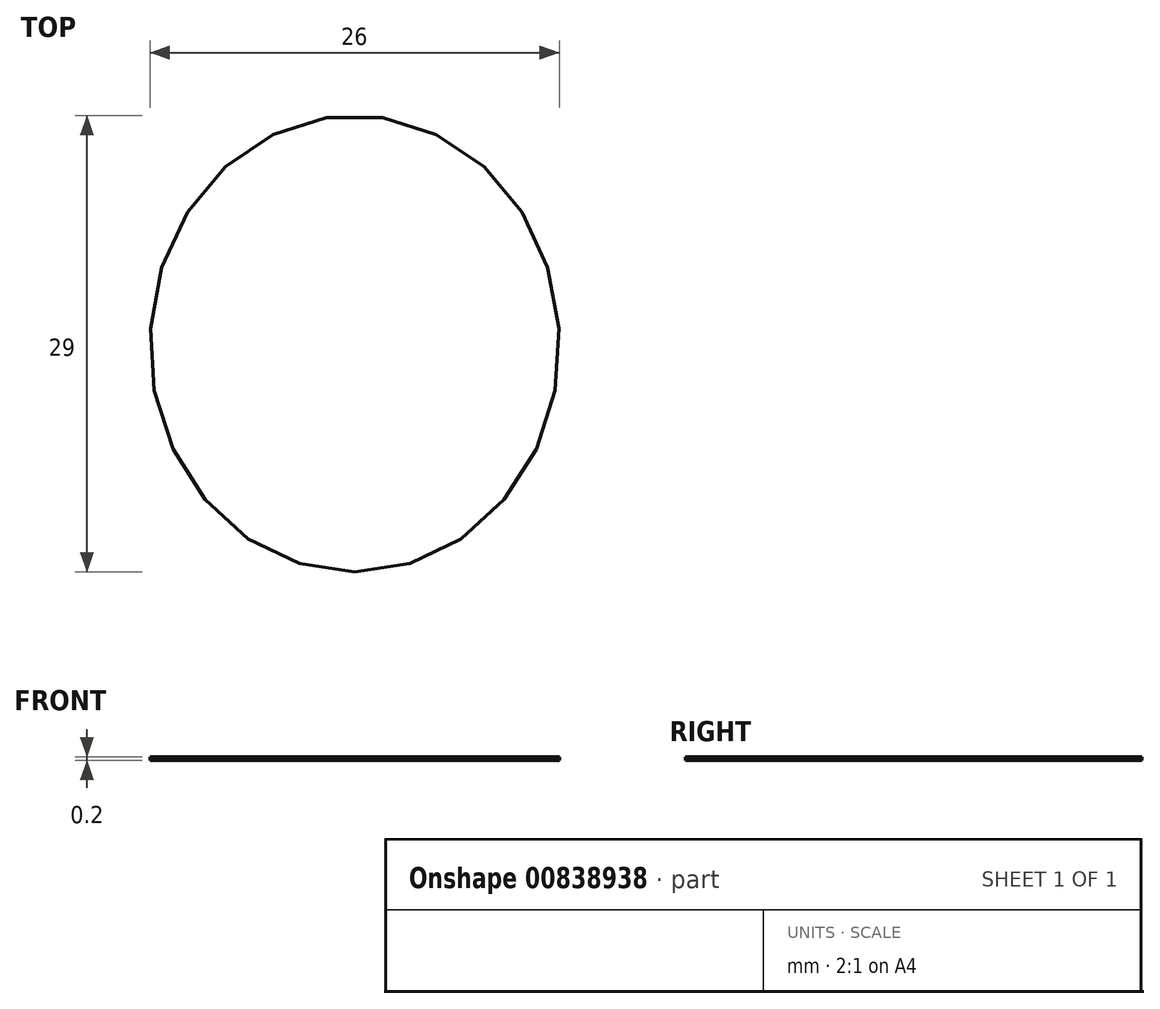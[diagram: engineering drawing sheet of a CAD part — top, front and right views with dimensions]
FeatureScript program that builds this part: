
annotation { "Feature Type Name" : "Feature", "Feature Type Description" : "" }
export const myFeature = defineFeature(function(context is Context, id is Id, definition is map)
    precondition{}
    {
        {
            var Q0;
            Q0=qCreatedBy(makeId("Top.planeOp"),FACE);
            var sketch = newSketch(context, id + "F0", { "sketchPlane" : qUnion([Q0])});
            skEllipse(sketch, "E0", {"center": v(0, 0) * mm, "majorRadius": 14.5 * mm, "minorRadius": 13 * mm, "majorAxis": v(0, -1)});
            skSolve(sketch);
        }
        {
            var Q0;
            Q0 = qSketchRegion(id + "F0", true);
            extrude(context, id + "F1", {"entities" : qUnion([Q0]), "depth" : 0.2 * mm, "offsetDistance" : 25 * mm});
        }
    });
